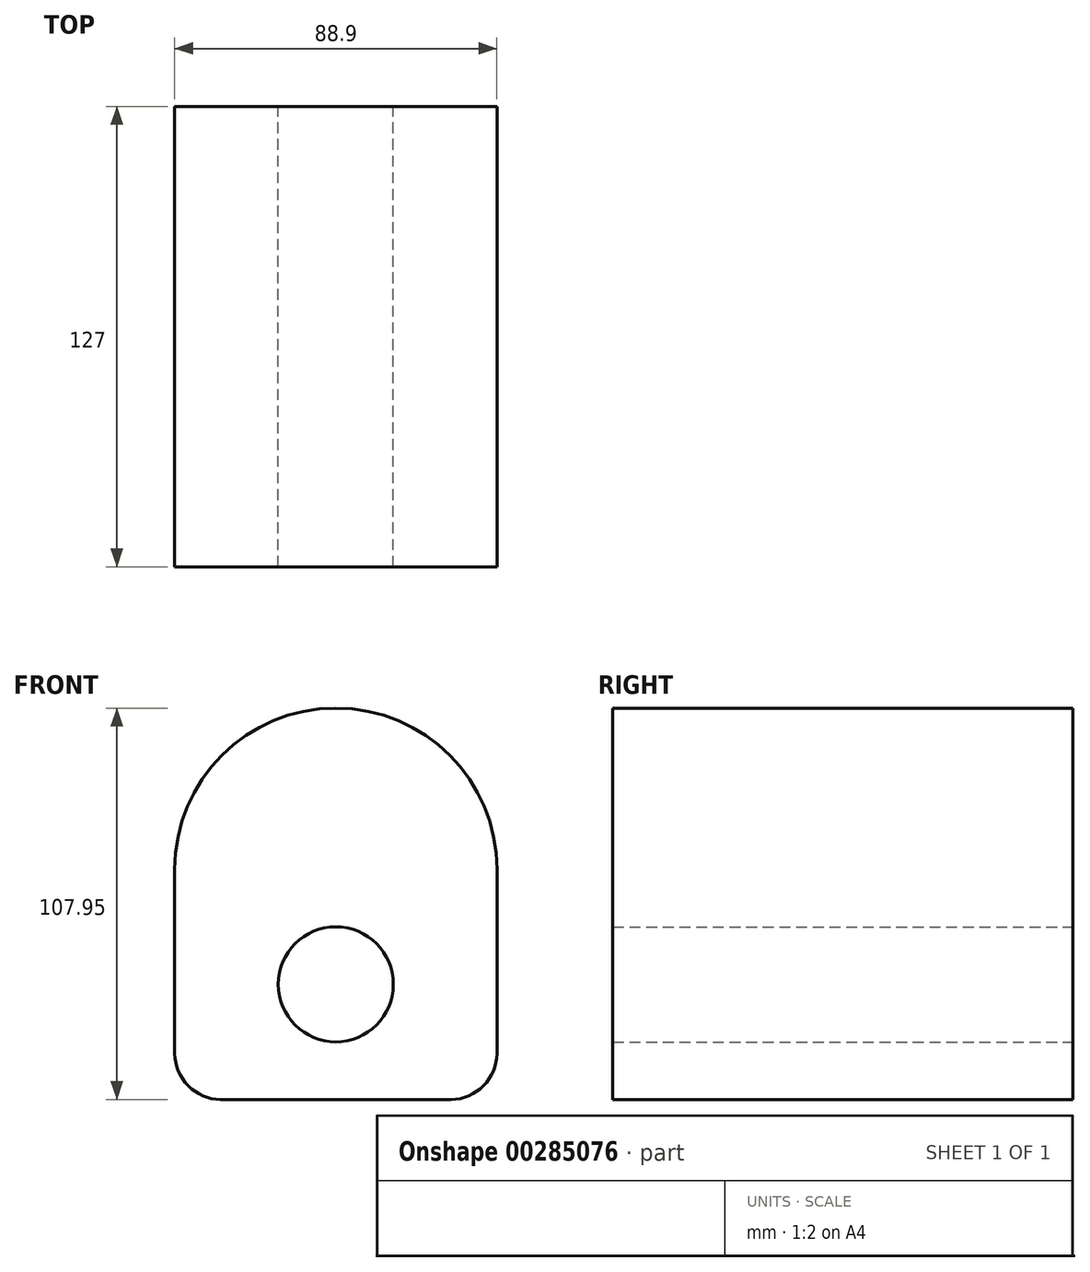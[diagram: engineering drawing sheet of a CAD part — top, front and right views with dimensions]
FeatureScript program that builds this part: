
annotation { "Feature Type Name" : "Feature", "Feature Type Description" : "" }
export const myFeature = defineFeature(function(context is Context, id is Id, definition is map)
    precondition{}
    {
        {
            var Q0;
            Q0=qCreatedBy(makeId("Front.planeOp"),FACE);
            var sketch = newSketch(context, id + "F0", { "sketchPlane" : qUnion([Q0])});
            skLineSegment(sketch, "E0.bottom", {"start": v(187.61, -122.79) * mm, "end": v(276.51, -122.79) * mm});
            skLineSegment(sketch, "E0.top", {"start": v(200.31, -186.29) * mm, "end": v(263.81, -186.29) * mm});
            skLineSegment(sketch, "E0.left", {"start": v(187.61, -122.79) * mm, "end": v(187.61, -173.59) * mm});
            skLineSegment(sketch, "E0.right", {"start": v(276.51, -122.79) * mm, "end": v(276.51, -173.59) * mm});
            skArc(sketch, "E1", {"start": v(276.51, -122.79) * mm, "mid": v(232.06, -78.34) * mm, "end": v(187.61, -122.79) * mm});
            skCircle(sketch, "E2", {"center": v(232.06, -154.54) * mm, "radius": 15.88 * mm});
            skPoint(sketch, "E2.centerSnap0", {"position": v(232.06, -186.29) * mm});
            skPoint(sketch, "E2.centerSnap1", {"position": v(187.61, -154.54) * mm});
            skPoint(sketch, "E3.visualSharp", {"position": v(187.61, -186.29) * mm});
            skArc(sketch, "E3.filletArc", {"start": v(187.61, -173.59) * mm, "mid": v(191.33, -182.57) * mm, "end": v(200.31, -186.29) * mm});
            skPoint(sketch, "E4.visualSharp", {"position": v(276.51, -186.29) * mm});
            skArc(sketch, "E4.filletArc", {"start": v(263.81, -186.29) * mm, "mid": v(272.8, -182.57) * mm, "end": v(276.51, -173.59) * mm});
            skSolve(sketch);
        }
        {
            var Q0;
            Q0=makeQuery(id+"F0.imprint","IMPRINT",FACE,{"disambiguationData":[TD([[makeQuery(id+"F0.imprint","IMPRINT",EDGE,{"derivedFrom":sQuery(id+"F0.wireOp",EDGE,"E0.bottom")}),-1.0]])]});
            var Q1;
            Q1=makeQuery(id+"F0.imprint","IMPRINT",FACE,{"disambiguationData":[TD([[makeQuery(id+"F0.imprint","IMPRINT",EDGE,{"derivedFrom":sQuery(id+"F0.wireOp",EDGE,"E0.bottom")}),1.0]])]});
            extrude(context, id + "F1", {"entities" : qUnion([Q0, Q1]), "depth" : 127 * mm});
        }
    });
